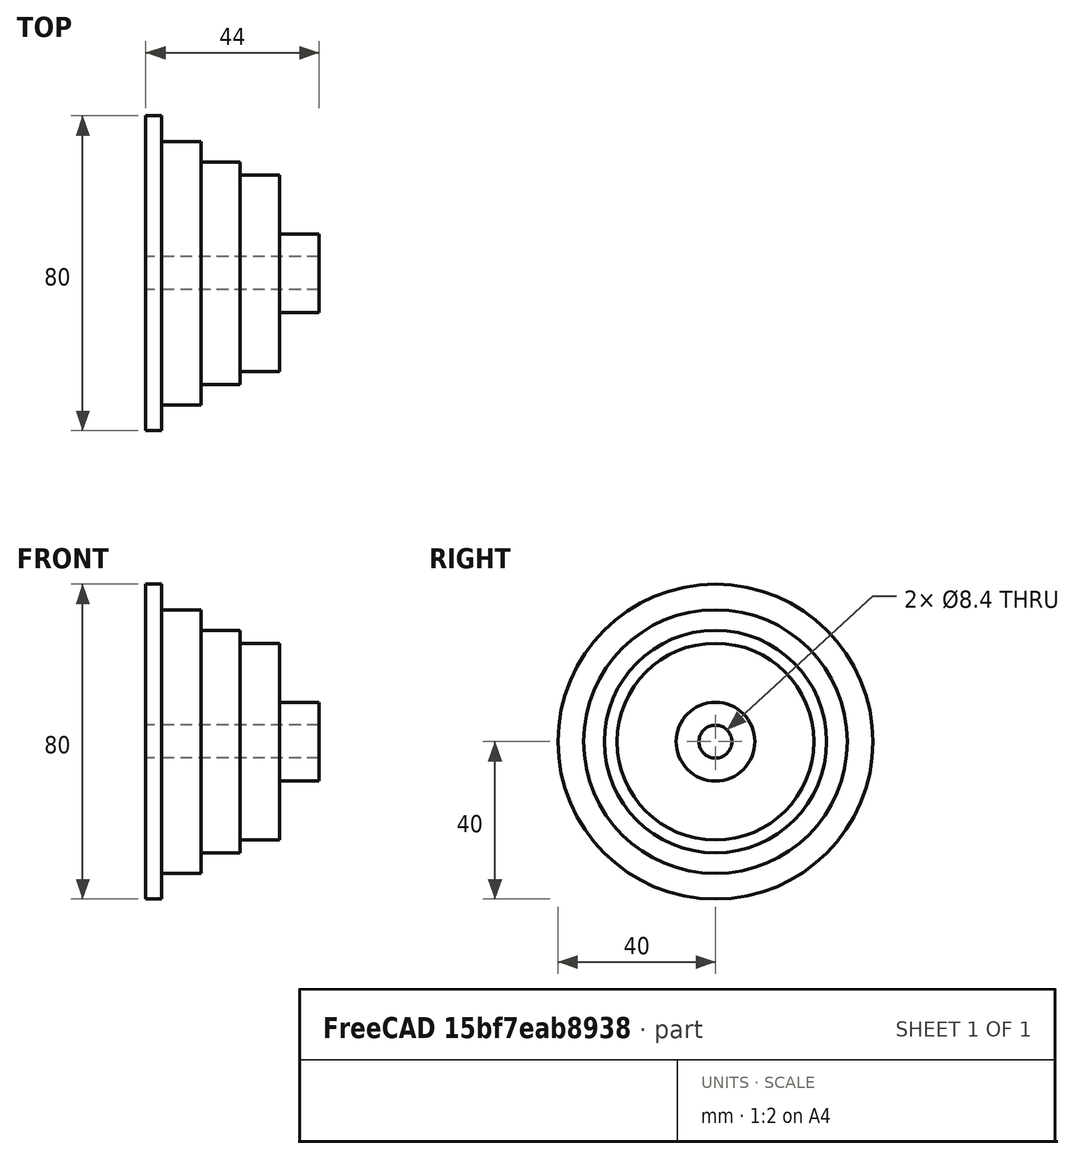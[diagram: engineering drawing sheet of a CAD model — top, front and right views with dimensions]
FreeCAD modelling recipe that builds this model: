
FCSTD DOCUMENT  (FreeCAD 0.17R13541 (Git))
Label: testFreeCad3
License: All rights reserved
LicenseURL: http://en.wikipedia.org/wiki/All_rights_reserved
objects: Sketcher::SketchObject×1, PartDesign::Revolution×1, PartDesign::Body×1
note: 4 computed .brp shape members not serialized (recipe doc carries the construction recipe); baked Part::Feature solids carry a one-line shape summary decoded from their .brp

FEATURE [Sketcher::SketchObject] Sketch
  MapMode = 5
  Support = -> [XY_Plane]
  sketch-geometry (15):
    g0: LineSegment StartX=43.188 StartY=30 StartZ=0 EndX=47.188 EndY=30 EndZ=0
    g1: LineSegment StartX=47.188 StartY=30 StartZ=0 EndX=47.188 EndY=23.5 EndZ=0
    g2: LineSegment StartX=47.188 StartY=23.5 StartZ=0 EndX=57.188 EndY=23.5 EndZ=0
    g3: LineSegment StartX=57.188 StartY=23.5 StartZ=0 EndX=57.188 EndY=18.25 EndZ=0
    g4: LineSegment StartX=57.188 StartY=18.25 StartZ=0 EndX=67.188 EndY=18.25 EndZ=0
    g5: LineSegment StartX=67.188 StartY=18.25 StartZ=0 EndX=67.188 EndY=15 EndZ=0
    g6: LineSegment StartX=67.188 StartY=15 StartZ=0 EndX=77.188 EndY=15 EndZ=0
    g7: LineSegment StartX=50 StartY=-5.8 StartZ=0 EndX=43.188 EndY=-5.8 EndZ=0
    g8: LineSegment StartX=43.188 StartY=-5.8 StartZ=0 EndX=43.188 EndY=30 EndZ=0
    g9: LineSegment [constr] StartX=-32.4069 StartY=-10 StartZ=0 EndX=67.5931 EndY=-10 EndZ=0
    g10: LineSegment StartX=77.188 StartY=5.65223 StartZ=0 EndX=77.188 EndY=0 EndZ=0
    g11: LineSegment StartX=77.188 StartY=0 StartZ=0 EndX=87.188 EndY=0 EndZ=0
    g12: LineSegment StartX=87.188 StartY=0 StartZ=0 EndX=87.188 EndY=-5.8 EndZ=0
    g13: LineSegment StartX=87.188 StartY=-5.8 StartZ=0 EndX=50 EndY=-5.8 EndZ=0
    g14: LineSegment StartX=77.188 StartY=15 StartZ=0 EndX=77.188 EndY=5.65223 EndZ=0
  constraints (41):
    c: Horizontal(g0)
    c: Coincident(g0,g1)
    c: Vertical(g1)
    c: Coincident(g1,g2)
    c: Horizontal(g2)
    c: Coincident(g2,g3)
    c: Vertical(g3)
    c: Coincident(g3,g4)
    c: Horizontal(g4)
    c: Coincident(g4,g5)
    c: Vertical(g5)
    c: Coincident(g5,g6)
    c: Horizontal(g6)
    c: Horizontal(g7)
    c: Coincident(g7,g8)
    c: Coincident(g8,g0)
    c: Vertical(g8)
    c: Horizontal(g9)
    c: DistanceY(g9,g0) = 40
    c: DistanceY(g9,g1) = 33.5
    c: DistanceY(g9,g3) = 28.25
    c: DistanceY(g9,g5) = 25
    c: PointOnObject(g10,g-1)
    c: Vertical(g10)
    c: Coincident(g10,g11)
    c: Horizontal(g11)
    c: Coincident(g11,g12)
    c: Vertical(g12)
    c: Coincident(g12,g13)
    c: Coincident(g13,g7)
    c: Horizontal(g13)
    c: DistanceY(g9,g10) = 10
    c: Coincident(g14,g6)
    c: Coincident(g14,g10)
    c: Vertical(g14)
    c: DistanceY(g9,g12) = 4.2
    c: DistanceX(g0,g0) = 4
    c: DistanceX(g2,g2) = 10
    c: Equal(g2,g4)
    c: Equal(g4,g6)
    c: Equal(g6,g11)
FEATURE [PartDesign::Revolution] Revolution
  Angle = 150
  Axis = (100,0,0)
  Base = (-32.4069,-10,0)
  Profile = -> Sketch
  ReferenceAxis = -> Sketch [Axis0]
FEATURE [PartDesign::Body] Body
  Group = -> [Sketch,Revolution]
  Origin = -> Origin
  Tip = -> Revolution
